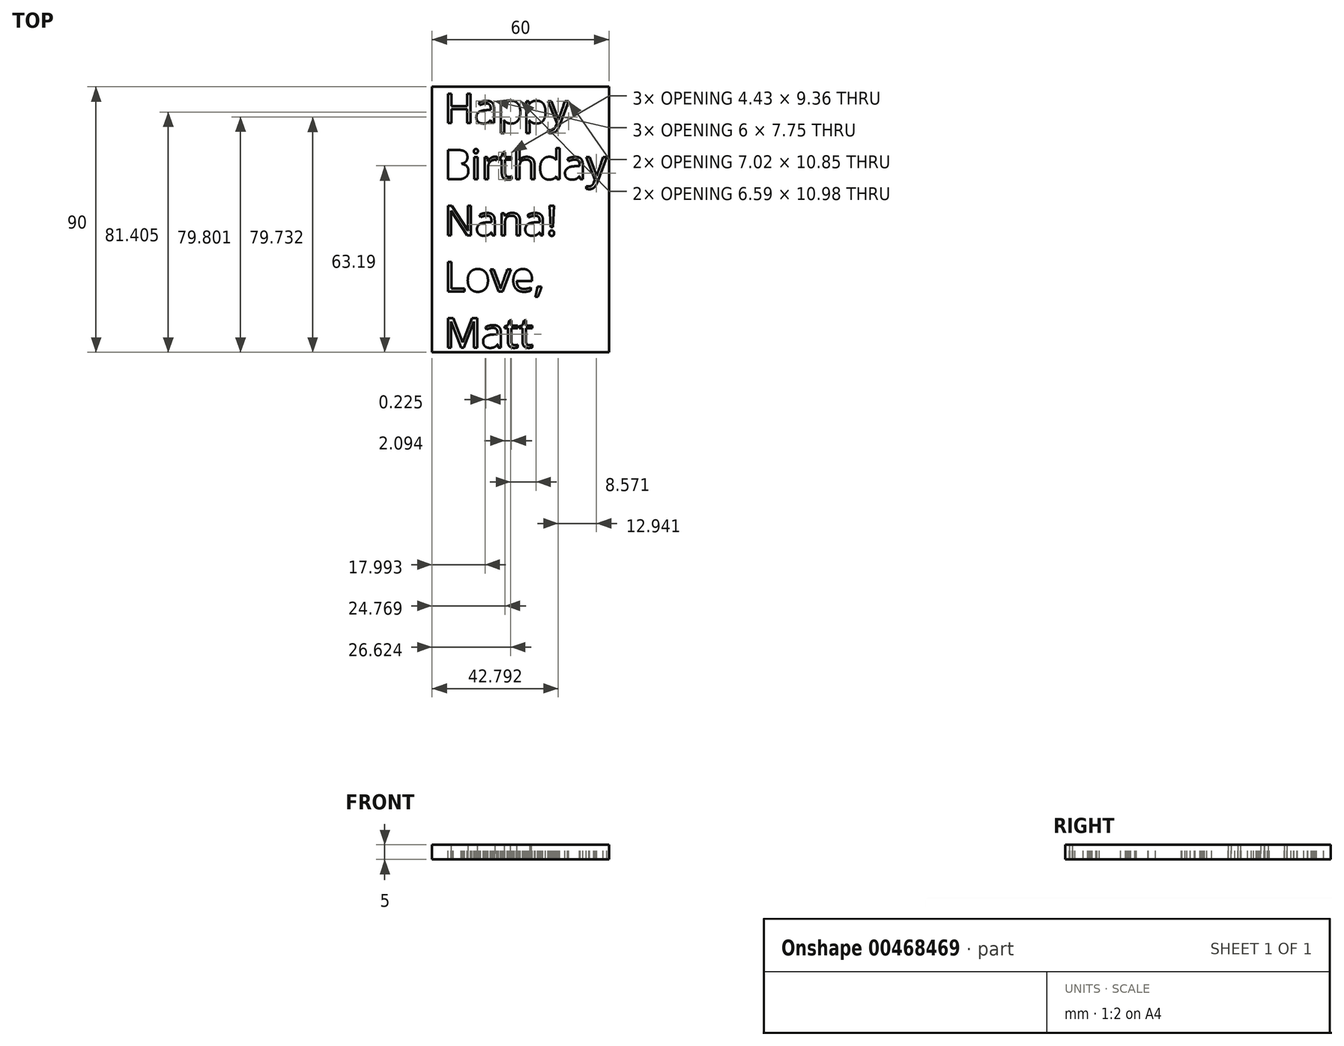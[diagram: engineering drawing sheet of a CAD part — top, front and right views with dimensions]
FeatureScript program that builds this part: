
annotation { "Feature Type Name" : "Feature", "Feature Type Description" : "" }
export const myFeature = defineFeature(function(context is Context, id is Id, definition is map)
    precondition{}
    {
        {
            var Q0;
            Q0=qCreatedBy(makeId("Top.planeOp"),FACE);
            var sketch = newSketch(context, id + "F0", { "sketchPlane" : qUnion([Q0])});
            skLineSegment(sketch, "E0.bottom", {"start": v(-24.23, 87.29) * mm, "end": v(35.77, 87.29) * mm});
            skLineSegment(sketch, "E0.top", {"start": v(-24.23, -2.71) * mm, "end": v(35.77, -2.71) * mm});
            skLineSegment(sketch, "E0.left", {"start": v(-24.23, 87.29) * mm, "end": v(-24.23, -2.71) * mm});
            skLineSegment(sketch, "E0.right", {"start": v(35.77, 87.29) * mm, "end": v(35.77, -2.71) * mm});
            skSolve(sketch);
        }
        {
            var Q0;
            Q0=makeQuery(id+"F0.imprint","IMPRINT",FACE,{"disambiguationData":[TD([[makeQuery(id+"F0.imprint","IMPRINT",EDGE,{"derivedFrom":sQuery(id+"F0.wireOp",EDGE,"E0.bottom")}),-1.0]])]});
            extrude(context, id + "F1", {"entities" : qUnion([Q0]), "depth" : 5 * mm});
        }
        {
            var Q0;
            Q0=makeQuery(id+"F1.opExtrude","CAP_FACE",FACE,{"disambiguationData":[OSD([sQuery(id+"F0.wireOp",EDGE,"E0.bottom"),sQuery(id+"F0.wireOp",EDGE,"E0.top"),sQuery(id+"F0.wireOp",EDGE,"E0.left"),sQuery(id+"F0.wireOp",EDGE,"E0.right")])],"isStart":false});
            var sketch = newSketch(context, id + "F2", { "sketchPlane" : qUnion([Q0])});
            skText(sketch, "E1", { "text": "Happy \nBirthday\nNana!\nLove,\nMatt", "fontName": "OpenSans-Regular.ttf"});
            const initialGuessF2  = {"E1": [-0.0202, 0.07496, 1, 0, 0.01007]};
            skSetInitialGuess(sketch, initialGuessF2);
            skSolve(sketch);
        }
        {
            var Q0;
            Q0 = qSketchRegion(id + "F2", true);
            extrude(context, id + "F3", {"entities" : qUnion([Q0]), "operationType" : NewBodyOperationType.REMOVE, "oppositeDirection" : true, "depth" : 25 * mm});
        }
        {
            var Q0;
            Q0=makeQuery(id+"F3.boolean.opBoolean","SPLIT",FACE,{"disambiguationData":[TD([makeQuery(id+"F3.opExtrude","SWEPT_FACE",FACE,{"disambiguationData":[OSD([sQuery(id+"F2.wireOp",EDGE,"E1.sketch_text.stroke-452")])]})])],"derivedFrom":makeQuery(id+"F1.opExtrude","CAP_FACE",FACE,{"disambiguationData":[OSD([sQuery(id+"F0.wireOp",EDGE,"E0.bottom"),sQuery(id+"F0.wireOp",EDGE,"E0.top"),sQuery(id+"F0.wireOp",EDGE,"E0.left"),sQuery(id+"F0.wireOp",EDGE,"E0.right")])],"isStart":false})});
            extrude(context, id + "F4", {"entities" : qUnion([Q0]), "operationType" : NewBodyOperationType.REMOVE, "oppositeDirection" : true, "depth" : 25 * mm});
        }
        {
            var Q0;
            Q0=makeQuery(id+"F3.boolean.opBoolean","SPLIT",FACE,{"disambiguationData":[TD([makeQuery(id+"F3.opExtrude","SWEPT_FACE",FACE,{"disambiguationData":[OSD([sQuery(id+"F2.wireOp",EDGE,"E1.sketch_text.stroke-403")])]})])],"derivedFrom":makeQuery(id+"F1.opExtrude","CAP_FACE",FACE,{"disambiguationData":[OSD([sQuery(id+"F0.wireOp",EDGE,"E0.bottom"),sQuery(id+"F0.wireOp",EDGE,"E0.top"),sQuery(id+"F0.wireOp",EDGE,"E0.left"),sQuery(id+"F0.wireOp",EDGE,"E0.right")])],"isStart":false})});
            extrude(context, id + "F5", {"entities" : qUnion([Q0]), "operationType" : NewBodyOperationType.REMOVE, "oppositeDirection" : true, "depth" : 25 * mm});
        }
        {
            var Q0;
            Q0=makeQuery(id+"F3.boolean.opBoolean","SPLIT",FACE,{"disambiguationData":[TD([makeQuery(id+"F3.opExtrude","SWEPT_FACE",FACE,{"disambiguationData":[OSD([sQuery(id+"F2.wireOp",EDGE,"E1.sketch_text.stroke-371")])]})])],"derivedFrom":makeQuery(id+"F1.opExtrude","CAP_FACE",FACE,{"disambiguationData":[OSD([sQuery(id+"F0.wireOp",EDGE,"E0.bottom"),sQuery(id+"F0.wireOp",EDGE,"E0.top"),sQuery(id+"F0.wireOp",EDGE,"E0.left"),sQuery(id+"F0.wireOp",EDGE,"E0.right")])],"isStart":false})});
            extrude(context, id + "F6", {"entities" : qUnion([Q0]), "operationType" : NewBodyOperationType.REMOVE, "oppositeDirection" : true, "depth" : 25 * mm});
        }
        {
            var Q0;
            Q0=makeQuery(id+"F3.boolean.opBoolean","SPLIT",FACE,{"disambiguationData":[TD([makeQuery(id+"F3.opExtrude","SWEPT_FACE",FACE,{"disambiguationData":[OSD([sQuery(id+"F2.wireOp",EDGE,"E1.sketch_text.stroke-116")])]})])],"derivedFrom":makeQuery(id+"F1.opExtrude","CAP_FACE",FACE,{"disambiguationData":[OSD([sQuery(id+"F0.wireOp",EDGE,"E0.bottom"),sQuery(id+"F0.wireOp",EDGE,"E0.top"),sQuery(id+"F0.wireOp",EDGE,"E0.left"),sQuery(id+"F0.wireOp",EDGE,"E0.right")])],"isStart":false})});
            extrude(context, id + "F7", {"entities" : qUnion([Q0]), "operationType" : NewBodyOperationType.REMOVE, "oppositeDirection" : true, "depth" : 25 * mm});
        }
        {
            var Q0;
            Q0=makeQuery(id+"F3.boolean.opBoolean","SPLIT",FACE,{"disambiguationData":[TD([makeQuery(id+"F3.opExtrude","SWEPT_FACE",FACE,{"disambiguationData":[OSD([sQuery(id+"F2.wireOp",EDGE,"E1.sketch_text.stroke-123")])]})])],"derivedFrom":makeQuery(id+"F1.opExtrude","CAP_FACE",FACE,{"disambiguationData":[OSD([sQuery(id+"F0.wireOp",EDGE,"E0.bottom"),sQuery(id+"F0.wireOp",EDGE,"E0.top"),sQuery(id+"F0.wireOp",EDGE,"E0.left"),sQuery(id+"F0.wireOp",EDGE,"E0.right")])],"isStart":false})});
            extrude(context, id + "F8", {"entities" : qUnion([Q0]), "operationType" : NewBodyOperationType.REMOVE, "oppositeDirection" : true, "depth" : 25 * mm});
        }
        {
            var Q0;
            Q0=makeQuery(id+"F3.boolean.opBoolean","SPLIT",FACE,{"disambiguationData":[TD([makeQuery(id+"F3.opExtrude","SWEPT_FACE",FACE,{"disambiguationData":[OSD([sQuery(id+"F2.wireOp",EDGE,"E1.sketch_text.stroke-207")])]})])],"derivedFrom":makeQuery(id+"F1.opExtrude","CAP_FACE",FACE,{"disambiguationData":[OSD([sQuery(id+"F0.wireOp",EDGE,"E0.bottom"),sQuery(id+"F0.wireOp",EDGE,"E0.top"),sQuery(id+"F0.wireOp",EDGE,"E0.left"),sQuery(id+"F0.wireOp",EDGE,"E0.right")])],"isStart":false})});
            extrude(context, id + "F9", {"entities" : qUnion([Q0]), "operationType" : NewBodyOperationType.REMOVE, "oppositeDirection" : true, "depth" : 25 * mm});
        }
        {
            var Q0;
            Q0=makeQuery(id+"F3.boolean.opBoolean","SPLIT",FACE,{"disambiguationData":[TD([makeQuery(id+"F3.opExtrude","SWEPT_FACE",FACE,{"disambiguationData":[OSD([sQuery(id+"F2.wireOp",EDGE,"E1.sketch_text.stroke-235")])]})])],"derivedFrom":makeQuery(id+"F1.opExtrude","CAP_FACE",FACE,{"disambiguationData":[OSD([sQuery(id+"F0.wireOp",EDGE,"E0.bottom"),sQuery(id+"F0.wireOp",EDGE,"E0.top"),sQuery(id+"F0.wireOp",EDGE,"E0.left"),sQuery(id+"F0.wireOp",EDGE,"E0.right")])],"isStart":false})});
            extrude(context, id + "F10", {"entities" : qUnion([Q0]), "operationType" : NewBodyOperationType.REMOVE, "oppositeDirection" : true, "depth" : 25 * mm});
        }
        {
            var Q0;
            Q0=makeQuery(id+"F3.boolean.opBoolean","SPLIT",FACE,{"disambiguationData":[TD([makeQuery(id+"F3.opExtrude","SWEPT_FACE",FACE,{"disambiguationData":[OSD([sQuery(id+"F2.wireOp",EDGE,"E1.sketch_text.stroke-55")])]})])],"derivedFrom":makeQuery(id+"F1.opExtrude","CAP_FACE",FACE,{"disambiguationData":[OSD([sQuery(id+"F0.wireOp",EDGE,"E0.bottom"),sQuery(id+"F0.wireOp",EDGE,"E0.top"),sQuery(id+"F0.wireOp",EDGE,"E0.left"),sQuery(id+"F0.wireOp",EDGE,"E0.right")])],"isStart":false})});
            extrude(context, id + "F11", {"entities" : qUnion([Q0]), "operationType" : NewBodyOperationType.REMOVE, "oppositeDirection" : true, "depth" : 25 * mm});
        }
        {
            var Q0;
            Q0=makeQuery(id+"F3.boolean.opBoolean","SPLIT",FACE,{"disambiguationData":[TD([makeQuery(id+"F3.opExtrude","SWEPT_FACE",FACE,{"disambiguationData":[OSD([sQuery(id+"F2.wireOp",EDGE,"E1.sketch_text.stroke-31")])]})])],"derivedFrom":makeQuery(id+"F1.opExtrude","CAP_FACE",FACE,{"disambiguationData":[OSD([sQuery(id+"F0.wireOp",EDGE,"E0.bottom"),sQuery(id+"F0.wireOp",EDGE,"E0.top"),sQuery(id+"F0.wireOp",EDGE,"E0.left"),sQuery(id+"F0.wireOp",EDGE,"E0.right")])],"isStart":false})});
            extrude(context, id + "F12", {"entities" : qUnion([Q0]), "operationType" : NewBodyOperationType.REMOVE, "oppositeDirection" : true, "depth" : 25 * mm});
        }
        {
            var Q0;
            Q0=makeQuery(id+"F3.boolean.opBoolean","SPLIT",FACE,{"disambiguationData":[TD([makeQuery(id+"F3.opExtrude","SWEPT_FACE",FACE,{"disambiguationData":[OSD([sQuery(id+"F2.wireOp",EDGE,"E1.sketch_text.stroke-80")])]})])],"derivedFrom":makeQuery(id+"F1.opExtrude","CAP_FACE",FACE,{"disambiguationData":[OSD([sQuery(id+"F0.wireOp",EDGE,"E0.bottom"),sQuery(id+"F0.wireOp",EDGE,"E0.top"),sQuery(id+"F0.wireOp",EDGE,"E0.left"),sQuery(id+"F0.wireOp",EDGE,"E0.right")])],"isStart":false})});
            extrude(context, id + "F13", {"entities" : qUnion([Q0]), "operationType" : NewBodyOperationType.REMOVE, "oppositeDirection" : true, "depth" : 25 * mm});
        }
        {
            var Q0;
            Q0=makeQuery(id+"F3.boolean.opBoolean","SPLIT",FACE,{"disambiguationData":[TD([makeQuery(id+"F3.opExtrude","SWEPT_FACE",FACE,{"disambiguationData":[OSD([sQuery(id+"F2.wireOp",EDGE,"E1.sketch_text.stroke-293")])]})])],"derivedFrom":makeQuery(id+"F1.opExtrude","CAP_FACE",FACE,{"disambiguationData":[OSD([sQuery(id+"F0.wireOp",EDGE,"E0.bottom"),sQuery(id+"F0.wireOp",EDGE,"E0.top"),sQuery(id+"F0.wireOp",EDGE,"E0.left"),sQuery(id+"F0.wireOp",EDGE,"E0.right")])],"isStart":false})});
            extrude(context, id + "F14", {"entities" : qUnion([Q0]), "operationType" : NewBodyOperationType.REMOVE, "oppositeDirection" : true, "depth" : 25 * mm});
        }
        {
            var Q0;
            Q0=makeQuery(id+"F3.boolean.opBoolean","SPLIT",FACE,{"disambiguationData":[TD([makeQuery(id+"F3.opExtrude","SWEPT_FACE",FACE,{"disambiguationData":[OSD([sQuery(id+"F2.wireOp",EDGE,"E1.sketch_text.stroke-337")])]})])],"derivedFrom":makeQuery(id+"F1.opExtrude","CAP_FACE",FACE,{"disambiguationData":[OSD([sQuery(id+"F0.wireOp",EDGE,"E0.bottom"),sQuery(id+"F0.wireOp",EDGE,"E0.top"),sQuery(id+"F0.wireOp",EDGE,"E0.left"),sQuery(id+"F0.wireOp",EDGE,"E0.right")])],"isStart":false})});
            extrude(context, id + "F15", {"entities" : qUnion([Q0]), "operationType" : NewBodyOperationType.REMOVE, "oppositeDirection" : true, "depth" : 25 * mm});
        }
        {
            var Q0;
            {var subQ0=sQuery(id+"F0.wireOp",EDGE,"E0.left");var subQ1=sQuery(id+"F0.wireOp",EDGE,"E0.bottom");var subQ2=sQuery(id+"F0.wireOp",EDGE,"E0.right");var subQ3=sQuery(id+"F0.wireOp",EDGE,"E0.top");Q0=makeQuery(id+"F3.boolean.opBoolean","SPLIT",FACE,{"disambiguationData":[TD([makeQuery(id+"F1.opExtrude","SWEPT_FACE",FACE,{"disambiguationData":[OSD([subQ1])]})])],"derivedFrom":makeQuery(id+"F1.opExtrude","CAP_FACE",FACE,{"disambiguationData":[OSD([subQ1,subQ3,subQ0,subQ2])],"isStart":false})});}
            extrude(context, id + "F16", {"entities" : qUnion([Q0]), "operationType" : NewBodyOperationType.REMOVE, "oppositeDirection" : true, "depth" : 3 * mm});
        }
        {
            var Q0;
            Q0=makeQuery(id+"F16.boolean.opBoolean","COPY",FACE,{"derivedFrom":makeQuery(id+"F16.opExtrude","CAP_FACE",FACE,{"disambiguationData":[OSD([sQuery(id+"F0.wireOp",EDGE,"E0.bottom"),sQuery(id+"F0.wireOp",EDGE,"E0.top"),sQuery(id+"F0.wireOp",EDGE,"E0.left"),sQuery(id+"F0.wireOp",EDGE,"E0.right")])],"isStart":false})});
            extrude(context, id + "F17", {"entities" : qUnion([Q0]), "operationType" : NewBodyOperationType.ADD, "depth" : 3 * mm});
        }
    });
